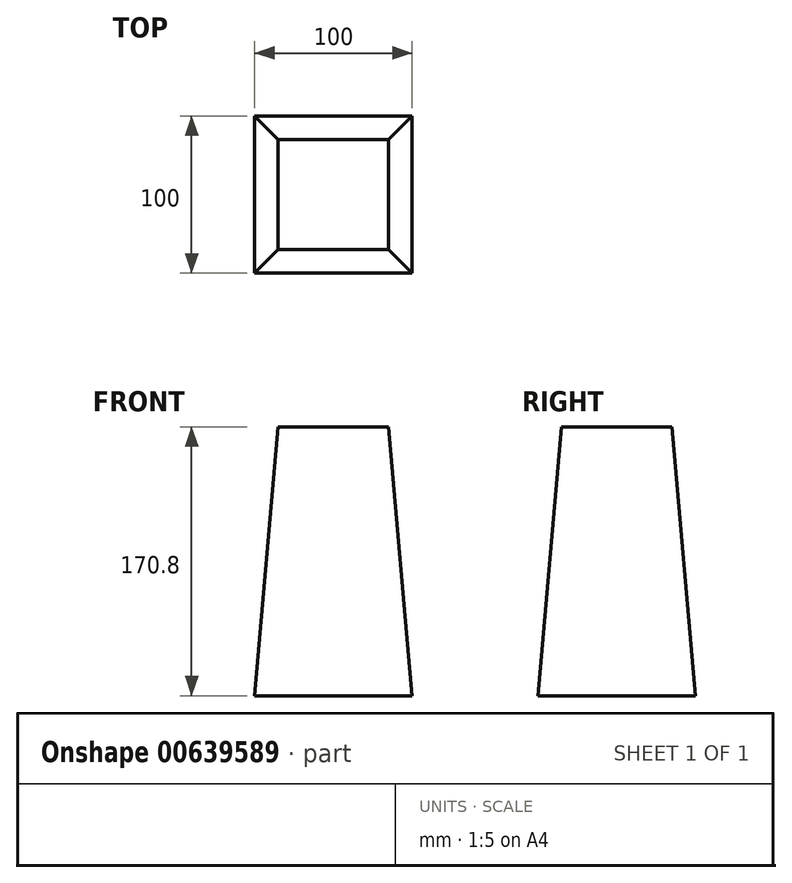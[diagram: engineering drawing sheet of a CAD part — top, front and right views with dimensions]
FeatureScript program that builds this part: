
annotation { "Feature Type Name" : "Feature", "Feature Type Description" : "" }
export const myFeature = defineFeature(function(context is Context, id is Id, definition is map)
    precondition{}
    {
        {
            var Q0;
            Q0=qCreatedBy(makeId("Top.planeOp"),FACE);
            var sketch = newSketch(context, id + "F0", { "sketchPlane" : qUnion([Q0])});
            skLineSegment(sketch, "E0.bottom", {"start": v(50, 50) * mm, "end": v(-50, 50) * mm});
            skLineSegment(sketch, "E0.top", {"start": v(50, -50) * mm, "end": v(-50, -50) * mm});
            skLineSegment(sketch, "E0.left", {"start": v(50, 50) * mm, "end": v(50, -50) * mm});
            skLineSegment(sketch, "E0.right", {"start": v(-50, 50) * mm, "end": v(-50, -50) * mm});
            skPoint(sketch, "E0.middle", {"position": v(0, 0) * mm});
            skSolve(sketch);
        }
        {
            var Q0;
            Q0 = qSketchRegion(id + "F0", true);
            extrude(context, id + "F1", {"entities" : qUnion([Q0]), "depth" : 74.8 * mm, "offsetDistance" : 25 * mm, "hasDraft" : true, "draftAngle" : 5 * degree, "draftPullDirection" : true});
        }
        {
            var Q0;
            Q0=makeQuery(id+"F1.opExtrude","CAP_FACE",FACE,{"disambiguationData":[OSD([sQuery(id+"F0.wireOp",EDGE,"E0.bottom"),sQuery(id+"F0.wireOp",EDGE,"E0.top"),sQuery(id+"F0.wireOp",EDGE,"E0.left"),sQuery(id+"F0.wireOp",EDGE,"E0.right")])],"isStart":false});
            extrude(context, id + "F2", {"entities" : qUnion([Q0]), "operationType" : NewBodyOperationType.ADD, "depth" : 96 * mm, "offsetDistance" : 25 * mm, "hasDraft" : true, "draftAngle" : 5 * degree, "draftPullDirection" : true});
        }
    });
